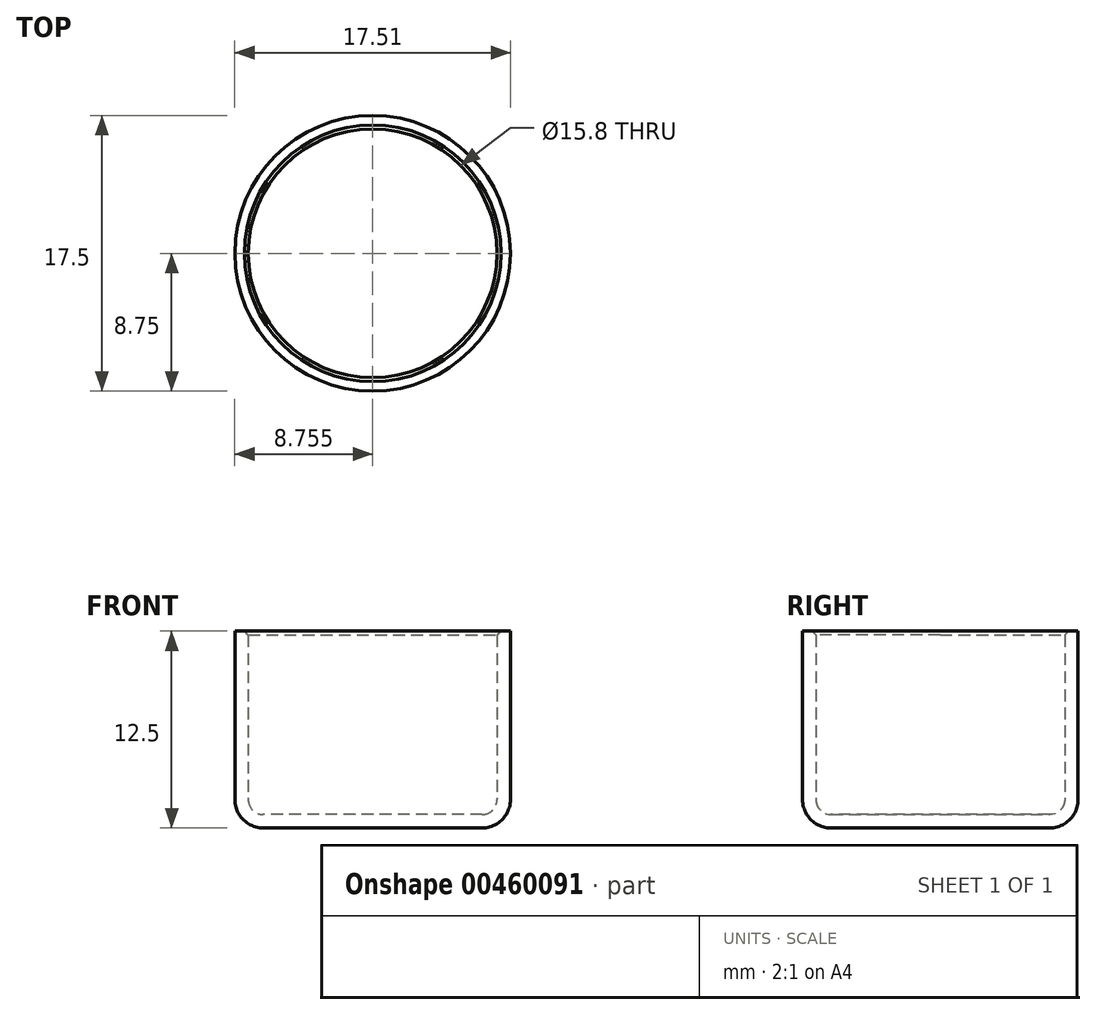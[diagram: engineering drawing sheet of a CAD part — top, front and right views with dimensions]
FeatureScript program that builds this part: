
annotation { "Feature Type Name" : "Feature", "Feature Type Description" : "" }
export const myFeature = defineFeature(function(context is Context, id is Id, definition is map)
    precondition{}
    {
        {
            var Q0;
            Q0=qCreatedBy(makeId("Front.planeOp"),FACE);
            var sketch = newSketch(context, id + "F0", { "sketchPlane" : qUnion([Q0])});
            skLineSegment(sketch, "E0.bottom", {"start": v(4.38, -6.25) * mm, "end": v(-4.38, -6.25) * mm});
            skLineSegment(sketch, "E0.top", {"start": v(4.37, 6.25) * mm, "end": v(-4.38, 6.25) * mm});
            skLineSegment(sketch, "E0.left", {"start": v(4.38, -6.25) * mm, "end": v(4.37, 6.25) * mm});
            skLineSegment(sketch, "E0.right", {"start": v(-4.38, -6.25) * mm, "end": v(-4.38, 6.25) * mm});
            skPoint(sketch, "E0.middle", {"position": v(0, 0) * mm});
            skSolve(sketch);
        }
        {
            var Q0;
            Q0=makeQuery(id+"F0.imprint","IMPRINT",FACE,{"disambiguationData":[TD([[makeQuery(id+"F0.imprint","IMPRINT",EDGE,{"derivedFrom":sQuery(id+"F0.wireOp",EDGE,"E0.bottom")}),-1.0]])]});
            var Q1;
            Q1=sQuery(id+"F0.wireOp",EDGE,"E0.right");
            revolve(context, id + "F1", {"entities" : qUnion([Q0]), "axis" : qUnion([Q1]), "revolveType" : RevolveType.FULL});
        }
        {
            var Q0;
            Q0=makeQuery(id+"F1.opRevolve","SWEPT_EDGE",EDGE,{"disambiguationData":[OSD([sQuery(id+"F0.wireOp",EDGE,"E0.bottom"),sQuery(id+"F0.wireOp",EDGE,"E0.left")])]});
            fillet(context, id + "F2", {"entities" : qUnion([Q0]), "radius" : 1.8 * mm, "tangentPropagation" : true, "allowEdgeOverflow" : false});
        }
        {
            var Q0;
            Q0=makeQuery(id+"F1.opRevolve","SWEPT_FACE",FACE,{"disambiguationData":[OSD([sQuery(id+"F0.wireOp",EDGE,"E0.top")])]});
            shell(context, id + "F3", {"entities" : qUnion([Q0]), "thickness" : 0.85 * mm});
        }
        {
            var Q0;
            Q0=makeQuery(id+"F3.opShell","OFFSET_EDGE",EDGE,{"disambiguationData":[OSD([sQuery(id+"F0.wireOp",EDGE,"E0.top"),sQuery(id+"F0.wireOp",EDGE,"E0.left")])]});
            chamfer(context, id + "F4", {"entities" : qUnion([Q0]), "width" : .25 * mm, "tangentPropagation" : true});
        }
    });
